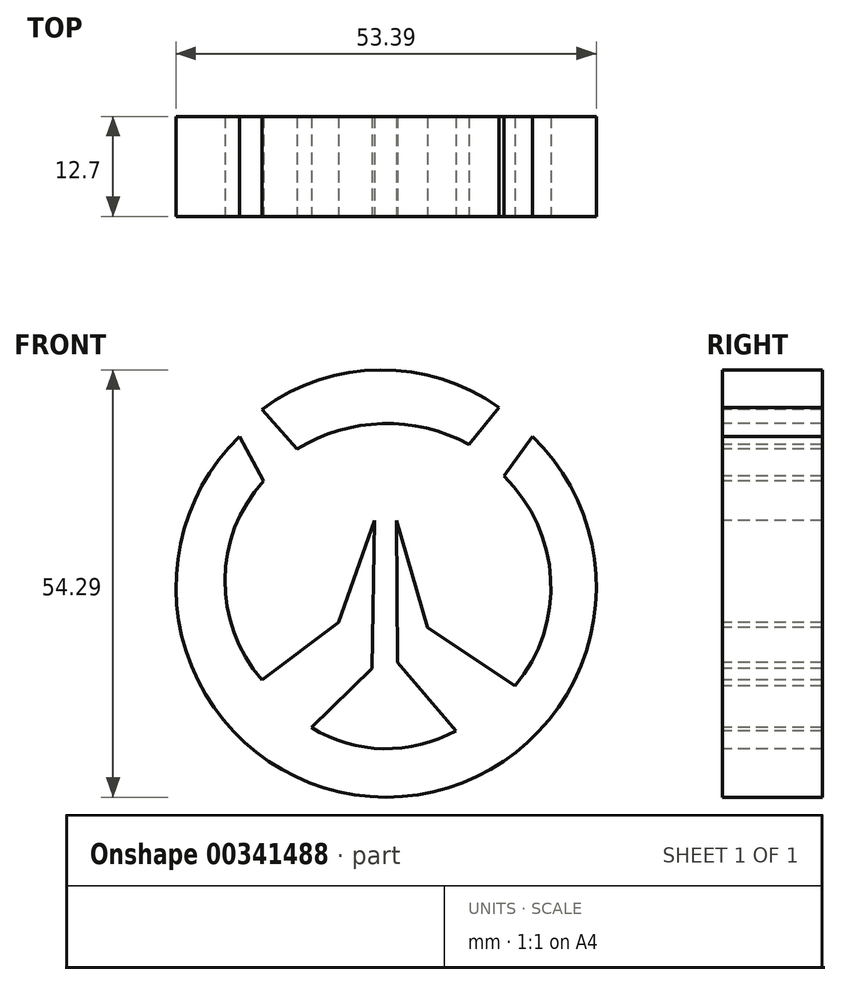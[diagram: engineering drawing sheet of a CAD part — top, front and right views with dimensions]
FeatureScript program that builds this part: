
annotation { "Feature Type Name" : "Feature", "Feature Type Description" : "" }
export const myFeature = defineFeature(function(context is Context, id is Id, definition is map)
    precondition{}
    {
        {
            var Q0;
            Q0=qCreatedBy(makeId("Front.planeOp"),FACE);
            var sketch = newSketch(context, id + "F0", { "sketchPlane" : qUnion([Q0])});
            skArc(sketch, "E0", {"start": v(-15.43, 14.73) * mm, "mid": v(-20.35, 2.14) * mm, "end": v(-15.63, -10.54) * mm});
            skArc(sketch, "E1", {"start": v(16.5, -11.35) * mm, "mid": v(21.04, 2.27) * mm, "end": v(15.1, 15.34) * mm});
            skArc(sketch, "E2", {"start": v(-9.37, -16.6) * mm, "mid": v(-0.22, -19.3) * mm, "end": v(9.03, -17) * mm});
            skArc(sketch, "E3", {"start": v(10.65, 19.38) * mm, "mid": v(-0.35, 22) * mm, "end": v(-11.18, 18.77) * mm});
            skArc(sketch, "E4", {"start": v(14.49, 24.03) * mm, "mid": v(-0.6, 28.84) * mm, "end": v(-15.63, 23.83) * mm});
            skArc(sketch, "E5", {"start": v(-18.46, 20.4) * mm, "mid": v(0.14, -25.45) * mm, "end": v(18.73, 20.4) * mm});
            skLineSegment(sketch, "E6", {"start": v(-5.93, -3.26) * mm, "end": v(-15.63, -10.54) * mm});
            skLineSegment(sketch, "E7", {"start": v(5.4, -3.87) * mm, "end": v(16.5, -11.35) * mm});
            skPoint(sketch, "E8.start.orphan", {"position": v(0, -8.72) * mm});
            skLineSegment(sketch, "E9", {"start": v(-1.37, 9.68) * mm, "end": v(-5.93, -3.26) * mm});
            skLineSegment(sketch, "E10", {"start": v(1.42, 9.68) * mm, "end": v(5.4, -3.87) * mm});
            skLineSegment(sketch, "E11", {"start": v(-1.68, -9.12) * mm, "end": v(-9.37, -16.6) * mm});
            skLineSegment(sketch, "E12", {"start": v(1.55, -8.31) * mm, "end": v(9.03, -17) * mm});
            skLineSegment(sketch, "E13", {"start": v(-18.46, 20.4) * mm, "end": v(-15.43, 14.73) * mm});
            skLineSegment(sketch, "E14", {"start": v(15.1, 15.34) * mm, "end": v(18.73, 20.4) * mm});
            skLineSegment(sketch, "E15", {"start": v(14.49, 24.03) * mm, "end": v(10.65, 19.38) * mm});
            skLineSegment(sketch, "E16", {"start": v(-15.63, 23.83) * mm, "end": v(-11.18, 18.77) * mm});
            skLineSegment(sketch, "E17", {"start": v(-1.37, 9.68) * mm, "end": v(1.42, 9.68) * mm});
            skLineSegment(sketch, "E18", {"start": v(1.55, -8.31) * mm, "end": v(-1.68, -9.12) * mm});
            skLineSegment(sketch, "E19", {"start": v(-1.68, -9.12) * mm, "end": v(-1.37, 9.68) * mm});
            skLineSegment(sketch, "E20", {"start": v(1.55, -8.31) * mm, "end": v(1.42, 9.68) * mm});
            skSolve(sketch);
        }
        {
            var Q0;
            Q0=makeQuery(id+"F0.imprint","IMPRINT",FACE,{"disambiguationData":[TD([[makeQuery(id+"F0.imprint","IMPRINT",EDGE,{"derivedFrom":sQuery(id+"F0.wireOp",EDGE,"E3")}),-1.0]])]});
            var Q1;
            Q1=makeQuery(id+"F0.imprint","IMPRINT",FACE,{"disambiguationData":[TD([[makeQuery(id+"F0.imprint","IMPRINT",EDGE,{"derivedFrom":sQuery(id+"F0.wireOp",EDGE,"E0")}),-1.0]])]});
            extrude(context, id + "F1", {"entities" : qUnion([Q0, Q1]), "oppositeDirection" : true, "depth" : 12.7 * mm});
        }
    });
